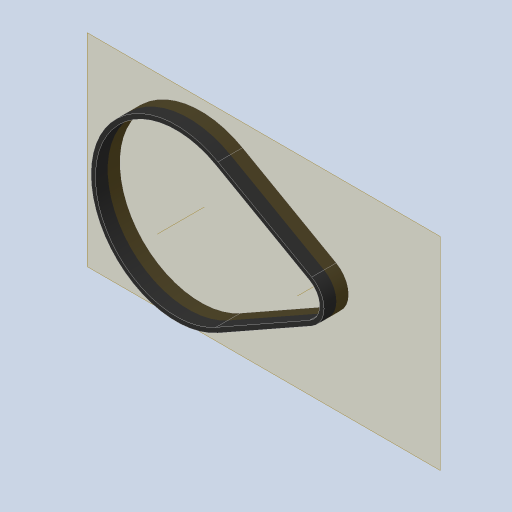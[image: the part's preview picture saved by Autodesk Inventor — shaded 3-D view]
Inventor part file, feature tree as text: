
AUTODESK INVENTOR PART (.ipt)
format: ipt  version: 2023.4 (Build 274418000, 418)  size: 172,032 bytes
history: native  units: in
note: dims shown in document units (in); Inventor stores cm internally (conversion verified against a paired STEP export)
features: sketch x3, extrude x1, other x1, projected_geometry x1
ambient origin geometry x8: Origin, YZ Plane, XZ Plane, XY Plane, X Axis, Y Axis, Z Axis, Center Point
bodies: Body1 (feature_tree)
feature tree (6):
  sketch  "Sketch2"  dims[d0=0.6015in d1=2.2558in]
  extrude  "Extrusion2"  Depth=2.2558in
  sketch  "Sketch5"  dims[d3=4.7032in d5=1.4644in d9=0.0787in d10=0.0598in d11=0.0299in d12=0.0219in d13=0.0219in d14=0.0059in d15=0.0059in d20=0.3346in d21=0.0in d22=0.0787in d23=0.0598in d24=0.0299in d25=0.0219in d26=0.0219in d27=0.0059in d28=0.0059in d29=0.0299in d30=0.0394in d31=0.0787in d32=0.0232in d34=0.0219in d35=0.0in d36=0.0in d37=0.0059in d38=0.0022in d39=0.0022in d40=0.0in d41=0.0in d42=0.0081in d43=0.0081in d44=0.0299in]
  other  "Work Axis1"
  sketch  "Sketch4"  dims[d2=0.6356in]
  projected_geometry  "Projected Loop1"
